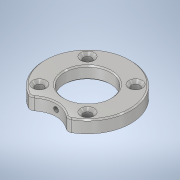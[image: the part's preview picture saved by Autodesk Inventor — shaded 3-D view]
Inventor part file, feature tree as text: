
AUTODESK INVENTOR PART (.ipt)
format: ipt  version: 2020.1 (Build 241239000, 239)  size: 215,040 bytes
history: native  units: mm
features: chamfer x3, fillet x2, sketch x2, projected_geometry x2, extrude x1, plane x1, hole x1, thread x1
ambient origin geometry x8: Origin, YZ Plane, XZ Plane, XY Plane, X Axis, Y Axis, Z Axis, Center Point
bodies: Solid1 (feature_tree)
feature tree (13):
  extrude  "Extrusion1"  Depth=3.3mm
  fillet  "Fillet1"  Radius=40.0mm
  fillet  "Fillet2"  [1 undecoded]
  chamfer  "Chamfer1"  Distance=15.0mm
  chamfer  "Chamfer2"  Distance=5.0mm
  chamfer  "Chamfer3"  Distance=2.0mm
  plane  "Work Plane1"
  hole  "Hole1"  [1 undecoded]
  thread  "Thread5"  [1 undecoded]
  sketch  "Sketch1"  dims[d0=18.5mm d2=3.3mm d4=40.0mm d6=360.0deg d8=45.0deg]
  sketch  "Sketch2"  dims[d10=19.0mm d11=15.0mm d12=5.0mm d13=0.0mm d14=2.0mm d15=1.0mm d24=0.5mm d25=2.0mm d26=45.0deg d27=0.0mm d30=8.0mm d32=0.5mm d33=2.0mm d34=45.0deg d36=27.5mm d37=1.1mm d38=2.0mm d39=45.0deg d40=2.5mm d41=5.0mm d42=2.5mm d43=2.0mm d44=6.0mm d45=4.0mm d46=2.0mm d47=90.0deg d48=8.0mm d49=0.0mm d50=3.516mm d51=0.0mm d52=0.0625mm d53=0.75mm d54=0.375mm]
  projected_geometry  "Projected Loop1"
  projected_geometry  "Projected Loop2"
note: 3 required parameter values undecoded (feature->parameter linkage not recoverable at this tier; creation-order binding heuristic only, values carry confidence <= 0.55)
